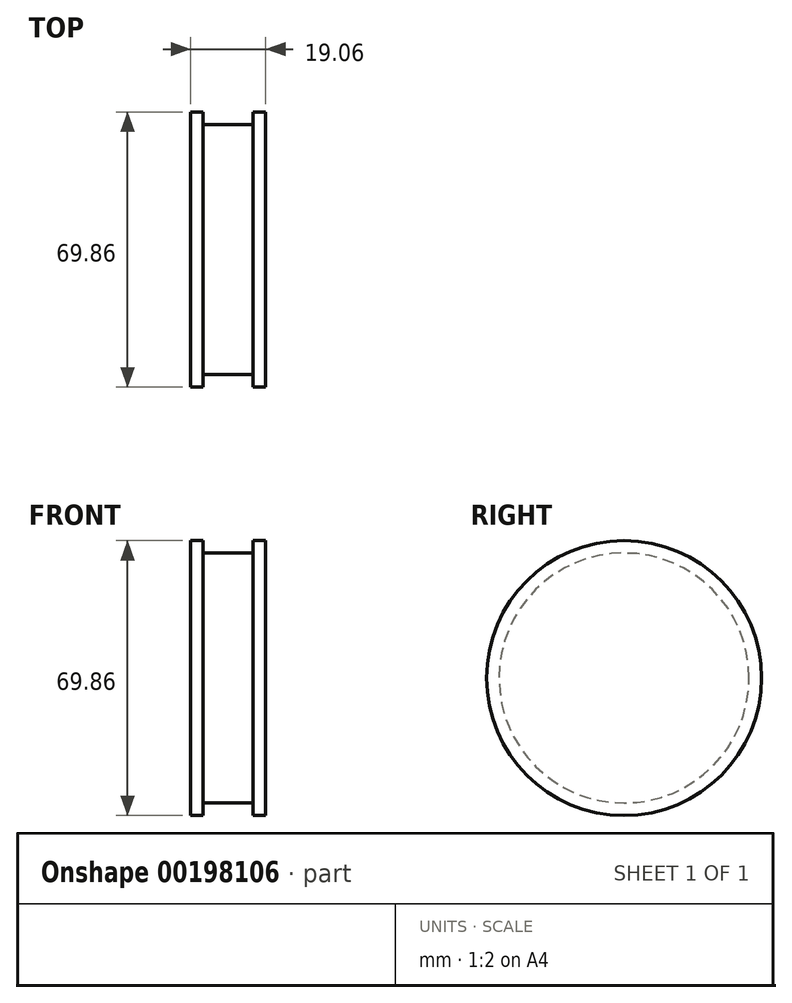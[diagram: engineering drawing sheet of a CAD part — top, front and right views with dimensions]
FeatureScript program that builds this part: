
annotation { "Feature Type Name" : "Feature", "Feature Type Description" : "" }
export const myFeature = defineFeature(function(context is Context, id is Id, definition is map)
    precondition{}
    {
        {
            var Q0;
            Q0=qCreatedBy(makeId("Right.planeOp"),FACE);
            var sketch = newSketch(context, id + "F0", { "sketchPlane" : qUnion([Q0])});
            skCircle(sketch, "E0", {"center": v(0, 0) * mm, "radius": 31.75 * mm});
            skSolve(sketch);
        }
        {
            var Q0;
            Q0=qSketchRegion(id+"F0",true);
            extrude(context, id + "F1", {"entities" : qUnion([Q0]), "endBound" : BoundingType.SYMMETRIC, "depth" : 12.7 * mm});
        }
        {
            var Q0;
            Q0=makeQuery(id+"F1.opExtrude","CAP_FACE",FACE,{"disambiguationData":[OSD([sQuery(id+"F0.wireOp",EDGE,"E0")])],"isStart":false});
            var sketch = newSketch(context, id + "F2", { "sketchPlane" : qUnion([Q0])});
            skCircle(sketch, "E1", {"center": v(0, 0) * mm, "radius": 34.93 * mm});
            skSolve(sketch);
        }
        {
            var Q0;
            Q0=qSketchRegion(id+"F2",true);
            extrude(context, id + "F3", {"entities" : qUnion([Q0]), "depth" : 3.17 * mm});
        }
        {
            var Q0;
            Q0=makeQuery(id+"F3.opExtrude","SWEPT_BODY",BODY,{"disambiguationData":[OSD([sQuery(id+"F2.wireOp",EDGE,"E1")])]});
            var Q1;
            Q1=qCreatedBy(makeId("Right.planeOp"),FACE);
            mirror(context, id + "F4", {"operationType" : NewBodyOperationType.ADD, "entities" : qUnion([Q0]), "mirrorPlane" : qUnion([Q1])});
        }
    });
